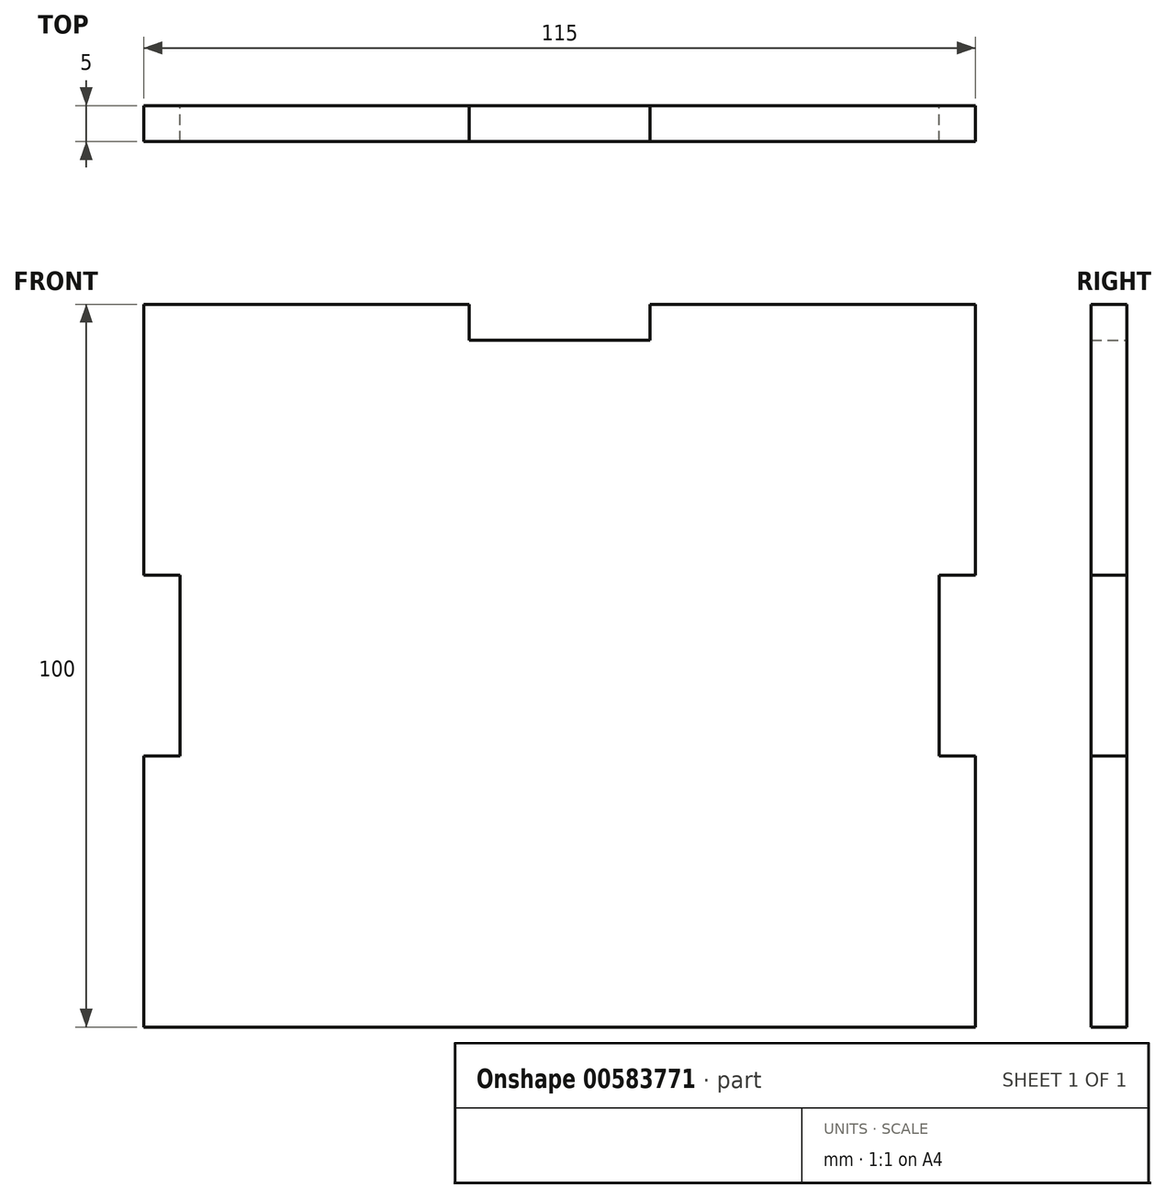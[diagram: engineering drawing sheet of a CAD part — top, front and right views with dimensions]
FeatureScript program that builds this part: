
annotation { "Feature Type Name" : "Feature", "Feature Type Description" : "" }
export const myFeature = defineFeature(function(context is Context, id is Id, definition is map)
    precondition{}
    {
        {
            var Q0;
            Q0=qCreatedBy(makeId("Front.planeOp"),FACE);
            var sketch = newSketch(context, id + "F0", { "sketchPlane" : qUnion([Q0])});
            skLineSegment(sketch, "E0", {"start": v(-70, 62.52) * mm, "end": v(-25, 62.52) * mm});
            skLineSegment(sketch, "E1", {"start": v(0, 62.52) * mm, "end": v(45, 62.52) * mm});
            skLineSegment(sketch, "E2", {"start": v(45, 62.52) * mm, "end": v(45, 25.02) * mm});
            skLineSegment(sketch, "E3", {"start": v(45, 0.02) * mm, "end": v(45, -37.48) * mm});
            skLineSegment(sketch, "E4", {"start": v(45, -37.48) * mm, "end": v(-70, -37.48) * mm});
            skLineSegment(sketch, "E5", {"start": v(-25, 62.52) * mm, "end": v(-25, 57.52) * mm});
            skLineSegment(sketch, "E6", {"start": v(-25, 57.52) * mm, "end": v(0, 57.52) * mm});
            skLineSegment(sketch, "E7", {"start": v(0, 57.52) * mm, "end": v(0, 62.52) * mm});
            skLineSegment(sketch, "E8", {"start": v(45, 25.02) * mm, "end": v(40, 25.02) * mm});
            skLineSegment(sketch, "E9", {"start": v(40, 25.02) * mm, "end": v(40, 0.02) * mm});
            skLineSegment(sketch, "E10", {"start": v(40, 0.02) * mm, "end": v(45, 0.02) * mm});
            skLineSegment(sketch, "E11", {"start": v(-70, 25.02) * mm, "end": v(-65, 25.02) * mm});
            skLineSegment(sketch, "E12", {"start": v(-65, 25.02) * mm, "end": v(-65, 0.02) * mm});
            skLineSegment(sketch, "E13", {"start": v(-65, 0.02) * mm, "end": v(-70, 0.02) * mm});
            skLineSegment(sketch, "E14", {"start": v(-70, 25.02) * mm, "end": v(-70, 62.52) * mm});
            skLineSegment(sketch, "E15", {"start": v(-70, 0.02) * mm, "end": v(-70, -37.48) * mm});
            skSolve(sketch);
        }
        {
            var Q0;
            Q0=makeQuery(id+"F0.imprint","IMPRINT",FACE,{"disambiguationData":[TD([[makeQuery(id+"F0.imprint","IMPRINT",EDGE,{"derivedFrom":sQuery(id+"F0.wireOp",EDGE,"E0")}),-1.0]])]});
            extrude(context, id + "F1", {"entities" : qUnion([Q0]), "depth" : 5 * mm, "offsetDistance" : 25 * mm});
        }
    });
